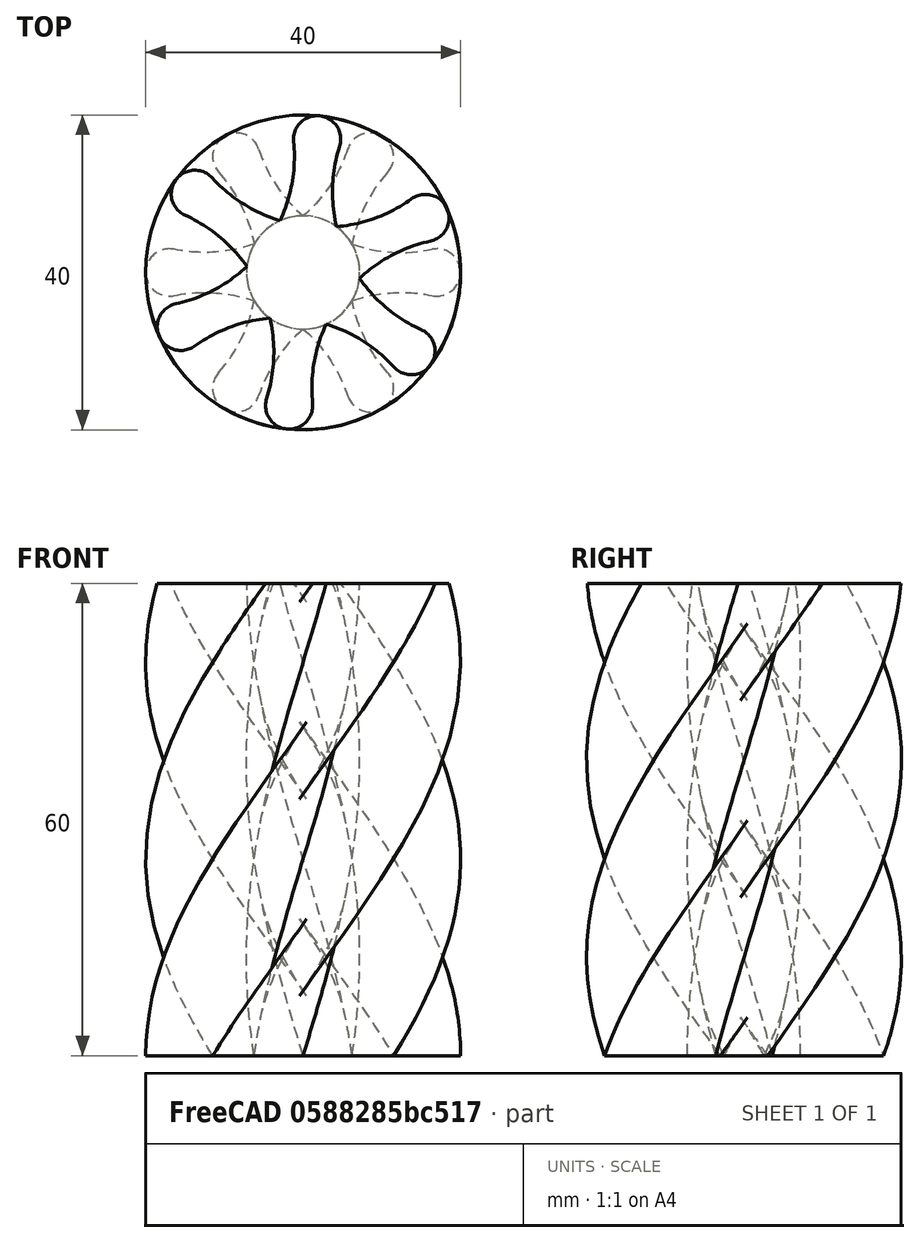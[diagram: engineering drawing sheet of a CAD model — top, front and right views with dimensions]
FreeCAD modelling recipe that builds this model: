
FCSTD DOCUMENT  (FreeCAD 0.21R33771 (Git))
Label: star
License: All rights reserved
LicenseURL: http://en.wikipedia.org/wiki/All_rights_reserved
objects: Sketcher::SketchObject×1, PartDesign::AdditiveHelix×1, PartDesign::Body×1
note: 4 computed .brp shape members not serialized (recipe doc carries the construction recipe); baked Part::Feature solids carry a one-line shape summary decoded from their .brp

FEATURE [Sketcher::SketchObject] Sketch
  FullyConstrained = true
  MapMode = 5
  Support = -> [XY_Plane]
  sketch-geometry (33):
    g0: LineSegment StartX=17 StartY=0 StartZ=0 EndX=8.5 EndY=14.7224 EndZ=0
    g1: LineSegment StartX=8.5 StartY=14.7224 StartZ=0 EndX=-8.5 EndY=14.7224 EndZ=0
    g2: LineSegment StartX=-8.5 StartY=14.7224 StartZ=0 EndX=-17 EndY=-1.8e-15 EndZ=0
    g3: LineSegment StartX=-17 StartY=-2.2e-15 StartZ=0 EndX=-8.5 EndY=-14.7224 EndZ=0
    g4: LineSegment StartX=-8.5 StartY=-14.7224 StartZ=0 EndX=8.5 EndY=-14.7224 EndZ=0
    g5: LineSegment StartX=8.5 StartY=-14.7224 StartZ=0 EndX=17 EndY=0 EndZ=0
    g6: Circle CenterX=0 CenterY=0 CenterZ=0 NormalX=0 NormalY=0 NormalZ=1 AngleXU=0 Radius=17
    g7: ArcOfCircle CenterX=-8.5 CenterY=14.7224 CenterZ=0 NormalX=0 NormalY=0 NormalZ=1 AngleXU=0 Radius=3 StartAngle=0.31867 EndAngle=3.87012
    g8: ArcOfCircle CenterX=8.5 CenterY=14.7224 CenterZ=0 NormalX=0 NormalY=0 NormalZ=1 AngleXU=0 Radius=3 StartAngle=5.55466 EndAngle=9.1061
    g9: ArcOfCircle CenterX=-17 CenterY=-2.2e-15 CenterZ=0 NormalX=0 NormalY=0 NormalZ=1 AngleXU=0 Radius=3 StartAngle=1.36587 EndAngle=4.91732
    g10: ArcOfCircle CenterX=-8.5 CenterY=-14.7224 CenterZ=0 NormalX=0 NormalY=0 NormalZ=1 AngleXU=0 Radius=3 StartAngle=2.41307 EndAngle=5.96452
    g11: ArcOfCircle CenterX=8.5 CenterY=-14.7224 CenterZ=0 NormalX=0 NormalY=0 NormalZ=1 AngleXU=0 Radius=3 StartAngle=3.46027 EndAngle=7.01171
    g12: ArcOfCircle CenterX=17 CenterY=0 CenterZ=0 NormalX=0 NormalY=0 NormalZ=1 AngleXU=0 Radius=3 StartAngle=4.50746 EndAngle=8.05891
    g13: Circle CenterX=0 CenterY=0 CenterZ=0 NormalX=0 NormalY=0 NormalZ=1 AngleXU=0 Radius=4
    g14: LineSegment StartX=25 StartY=0 StartZ=0 EndX=12.5 EndY=21.6506 EndZ=0
    g15: LineSegment StartX=12.5 StartY=21.6506 StartZ=0 EndX=-12.5 EndY=21.6506 EndZ=0
    g16: LineSegment StartX=-12.5 StartY=21.6506 StartZ=0 EndX=-25 EndY=0 EndZ=0
    g17: LineSegment StartX=-25 StartY=-5e-16 StartZ=0 EndX=-12.5 EndY=-21.6506 EndZ=0
    g18: LineSegment StartX=-12.5 StartY=-21.6506 StartZ=0 EndX=12.5 EndY=-21.6506 EndZ=0
    g19: LineSegment StartX=12.5 StartY=-21.6506 StartZ=0 EndX=25 EndY=0 EndZ=0
    g20: Circle CenterX=0 CenterY=0 CenterZ=0 NormalX=0 NormalY=0 NormalZ=1 AngleXU=0 Radius=25
    g21: ArcOfCircle CenterX=-12.5 CenterY=21.6506 CenterZ=0 NormalX=0 NormalY=0 NormalZ=1 AngleXU=0 Radius=19.1133 StartAngle=4.50746 EndAngle=5.04674
    g22: ArcOfCircle CenterX=-12.5 CenterY=-21.6506 CenterZ=0 NormalX=0 NormalY=0 NormalZ=1 AngleXU=0 Radius=19.1133 StartAngle=0.31867 EndAngle=0.857945
    g23: ArcOfCircle CenterX=12.5 CenterY=-21.6506 CenterZ=0 NormalX=0 NormalY=0 NormalZ=1 AngleXU=0 Radius=19.1133 StartAngle=1.36587 EndAngle=1.90514
    g24: ArcOfCircle CenterX=-25 CenterY=-5e-16 CenterZ=0 NormalX=0 NormalY=0 NormalZ=1 AngleXU=0 Radius=19.1133 StartAngle=5.55466 EndAngle=6.09393
    g25: ArcOfCircle CenterX=12.5 CenterY=21.6506 CenterZ=0 NormalX=0 NormalY=0 NormalZ=1 AngleXU=0 Radius=19.1133 StartAngle=3.46026 EndAngle=3.99954
    g26: ArcOfCircle CenterX=25 CenterY=0 CenterZ=0 NormalX=0 NormalY=0 NormalZ=1 AngleXU=0 Radius=19.1133 StartAngle=2.41307 EndAngle=2.95234
    g27: ArcOfCircle CenterX=-25 CenterY=-5e-16 CenterZ=0 NormalX=0 NormalY=0 NormalZ=1 AngleXU=0 Radius=19.1133 StartAngle=0.189252 EndAngle=0.728528
    g28: ArcOfCircle CenterX=-12.5 CenterY=21.6506 CenterZ=0 NormalX=0 NormalY=0 NormalZ=1 AngleXU=0 Radius=19.1133 StartAngle=5.42524 EndAngle=5.96452
    g29: ArcOfCircle CenterX=12.5 CenterY=21.6506 CenterZ=0 NormalX=0 NormalY=0 NormalZ=1 AngleXU=0 Radius=19.1133 StartAngle=4.37804 EndAngle=4.91732
    g30: ArcOfCircle CenterX=25 CenterY=0 CenterZ=0 NormalX=0 NormalY=0 NormalZ=1 AngleXU=0 Radius=19.1133 StartAngle=3.33085 EndAngle=3.87012
    g31: ArcOfCircle CenterX=-12.5 CenterY=-21.6506 CenterZ=0 NormalX=0 NormalY=0 NormalZ=1 AngleXU=0 Radius=19.1133 StartAngle=1.23645 EndAngle=1.77572
    g32: ArcOfCircle CenterX=12.5 CenterY=-21.6506 CenterZ=0 NormalX=0 NormalY=0 NormalZ=1 AngleXU=0 Radius=19.1133 StartAngle=2.28365 EndAngle=2.82292
  constraints (83):
    c: Coincident(g0,g1)
    c: Coincident(g1,g2)
    c: Coincident(g2,g3)
    c: Coincident(g3,g4)
    c: Coincident(g4,g5)
    c: Coincident(g5,g0)
    c: Equal(g0, g1-g5) x5
    c: PointOnObject(g0,g6)
    c: PointOnObject(g1,g6)
    c: PointOnObject(g2,g6)
    c: PointOnObject(g3,g6)
    c: PointOnObject(g4,g6)
    c: PointOnObject(g5,g6)
    c: Coincident(g6,g-1)
    c: PointOnObject(g5,g-1)
    c: Radius(g6) = 17
    c: Coincident(g7,g1)
    c: Coincident(g8,g0)
    c: Coincident(g9,g2)
    c: Coincident(g10,g3)
    c: Coincident(g11,g4)
    c: Coincident(g12,g0)
    c: Equal(g7,g9)
    c: Equal(g9,g10)
    c: Equal(g11,g7)
    c: Equal(g12,g7)
    c: Equal(g8,g7)
    c: Radius(g7) = 3
    c: Coincident(g13,g6)
    c: Radius(g13) = 4
    c: Coincident(g14,g15)
    c: Coincident(g15,g16)
    c: Coincident(g16,g17)
    c: Coincident(g17,g18)
    c: Coincident(g18,g19)
    c: Coincident(g19,g14)
    c: Equal(g14, g15-g19) x5
    c: PointOnObject(g14,g20)
    c: PointOnObject(g15,g20)
    c: PointOnObject(g16,g20)
    c: PointOnObject(g17,g20)
    c: PointOnObject(g18,g20)
    c: PointOnObject(g19,g20)
    c: Coincident(g20,g13)
    c: PointOnObject(g19,g-1)
    c: Radius(g20) = 25
    c: Coincident(g21,g15)
    c: Tangent(g9,g22)
    c: Coincident(g22,g17)
    c: Coincident(g23,g18)
    c: Coincident(g24,g16)
    c: Coincident(g25,g14)
    c: Coincident(g26,g14)
    c: Equal(g24,g27)
    c: Coincident(g24,g27)
    c: Equal(g21,g28)
    c: Coincident(g21,g27)
    c: Coincident(g21,g28)
    c: Equal(g25,g29)
    c: Coincident(g25,g28)
    c: Coincident(g25,g29)
    c: Equal(g26,g30)
    c: Coincident(g26,g29)
    c: Coincident(g26,g30)
    c: Equal(g22,g31)
    c: Coincident(g31,g24)
    c: Coincident(g22,g31)
    c: Equal(g23,g32)
    c: Coincident(g23,g30)
    c: Coincident(g32,g22)
    c: Coincident(g23,g32)
    c: Tangent(g21,g9) = 1.5708
    c: Coincident(g31,g9)
    c: Tangent(g24,g10) = 1.5708
    c: Coincident(g32,g10)
    c: Coincident(g22,g11)
    c: Coincident(g30,g11)
    c: Tangent(g23,g12) = 1.5708
    c: Coincident(g29,g12)
    c: Coincident(g28,g8)
    c: Tangent(g26,g8) = 1.5708
    c: Coincident(g27,g7)
    c: Tangent(g25,g7) = 1.5708
FEATURE [PartDesign::AdditiveHelix] AdditiveHelix
  Angle = 0
  Axis = (0,0,1)
  Base = (0,0,0)
  Growth = 0
  HasBeenEdited = true
  Height = 60
  LeftHanded = false
  Mode = 0
  Outside = false
  Pitch = 150
  Profile = -> Sketch
  ReferenceAxis = -> Sketch [N_Axis]
  Turns = 0.4
FEATURE [PartDesign::Body] Body
  Group = -> [Sketch,AdditiveHelix]
  Origin = -> Origin
  Tip = -> AdditiveHelix
